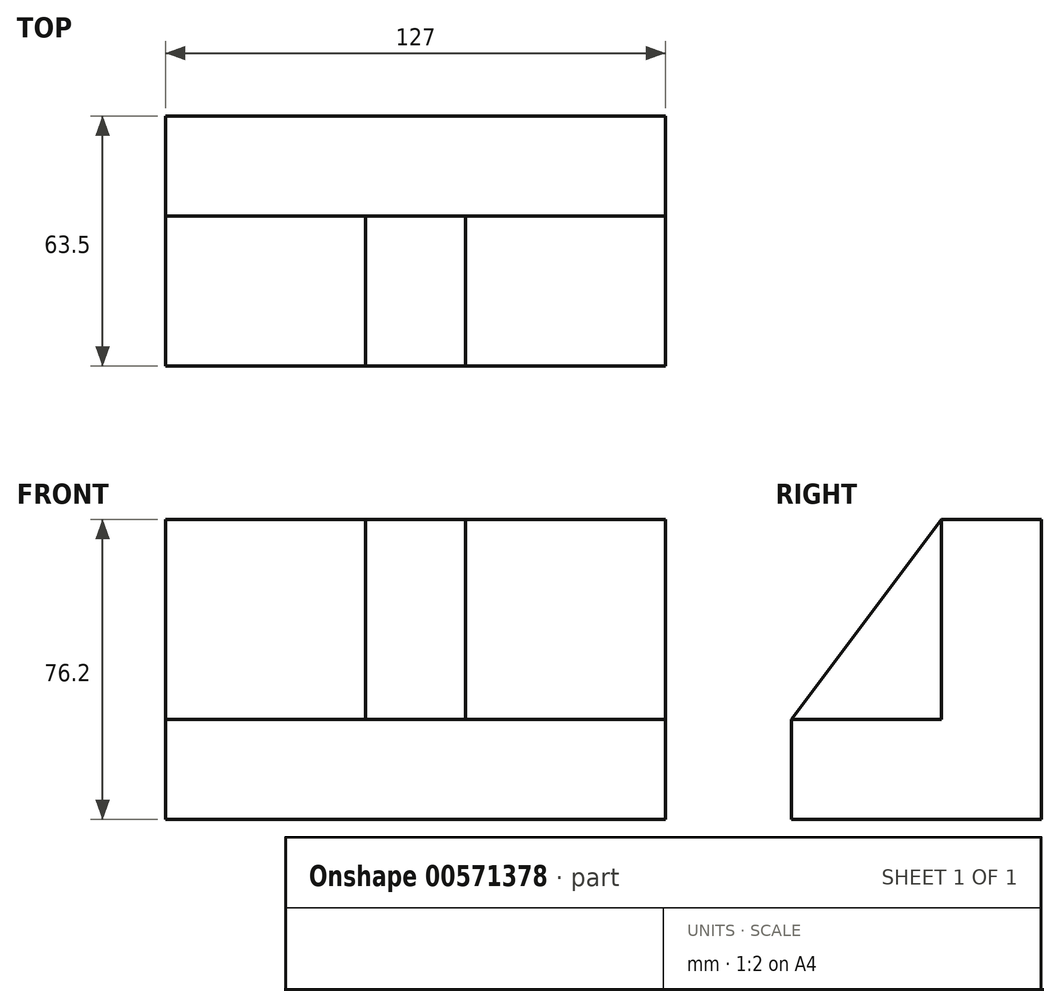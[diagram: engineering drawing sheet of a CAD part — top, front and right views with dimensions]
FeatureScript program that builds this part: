
annotation { "Feature Type Name" : "Feature", "Feature Type Description" : "" }
export const myFeature = defineFeature(function(context is Context, id is Id, definition is map)
    precondition{}
    {
        {
            var Q0;
            Q0=qCreatedBy(makeId("Front.planeOp"),FACE);
            var sketch = newSketch(context, id + "F0", { "sketchPlane" : qUnion([Q0])});
            skLineSegment(sketch, "E0.bottom", {"start": v(-94.95, 20.05) * mm, "end": v(32.05, 20.05) * mm});
            skLineSegment(sketch, "E0.top", {"start": v(-94.95, -56.15) * mm, "end": v(32.05, -56.15) * mm});
            skLineSegment(sketch, "E0.left", {"start": v(-94.95, 20.05) * mm, "end": v(-94.95, -56.15) * mm});
            skLineSegment(sketch, "E0.right", {"start": v(32.05, 20.05) * mm, "end": v(32.05, -56.15) * mm});
            skSolve(sketch);
        }
        {
            var Q0;
            Q0=makeQuery(id+"F0.imprint","IMPRINT",FACE,{"disambiguationData":[TD([[makeQuery(id+"F0.imprint","IMPRINT",EDGE,{"derivedFrom":sQuery(id+"F0.wireOp",EDGE,"E0.bottom")}),-1.0]])]});
            extrude(context, id + "F1", {"entities" : qUnion([Q0]), "depth" : 63.5 * mm, "offsetDistance" : 25.4 * mm});
        }
        {
            var Q0;
            Q0=makeQuery(id+"F1.opExtrude","SWEPT_FACE",FACE,{"disambiguationData":[OSD([sQuery(id+"F0.wireOp",EDGE,"E0.right")])]});
            var sketch = newSketch(context, id + "F2", { "sketchPlane" : qUnion([Q0])});
            skLineSegment(sketch, "E1", {"start": v(0, 20.05) * mm, "end": v(-25.4, 20.05) * mm});
            skLineSegment(sketch, "E2", {"start": v(-25.4, 20.05) * mm, "end": v(-25.4, -30.75) * mm});
            skLineSegment(sketch, "E3", {"start": v(-25.4, -30.75) * mm, "end": v(-63.5, -30.75) * mm});
            skPoint(sketch, "E3.endSnap0", {"position": v(-63.5, -18.05) * mm});
            skLineSegment(sketch, "E4", {"start": v(-63.5, -30.75) * mm, "end": v(-63.5, 20.05) * mm});
            skLineSegment(sketch, "E5", {"start": v(-63.5, 20.05) * mm, "end": v(-25.4, 20.05) * mm});
            skSolve(sketch);
        }
        {
            var Q0;
            Q0=makeQuery(id+"F2.imprint","IMPRINT",FACE,{"disambiguationData":[TD([[makeQuery(id+"F2.imprint","IMPRINT",EDGE,{"derivedFrom":sQuery(id+"F2.wireOp",EDGE,"E2")}),-1.0]])]});
            extrude(context, id + "F3", {"entities" : qUnion([Q0]), "operationType" : NewBodyOperationType.REMOVE, "oppositeDirection" : true, "depth" : 50.8 * mm, "offsetDistance" : 25.4 * mm});
        }
        {
            var Q0;
            Q0=makeQuery(id+"F1.opExtrude","SWEPT_FACE",FACE,{"disambiguationData":[OSD([sQuery(id+"F0.wireOp",EDGE,"E0.left")])]});
            var sketch = newSketch(context, id + "F4", { "sketchPlane" : qUnion([Q0])});
            skLineSegment(sketch, "E6", {"start": v(0, 20.05) * mm, "end": v(25.4, 20.05) * mm});
            skLineSegment(sketch, "E7", {"start": v(25.4, 20.05) * mm, "end": v(25.4, -30.75) * mm});
            skLineSegment(sketch, "E8", {"start": v(25.4, -30.75) * mm, "end": v(63.5, -30.75) * mm});
            skLineSegment(sketch, "E9", {"start": v(63.5, -30.75) * mm, "end": v(63.5, 20.05) * mm});
            skLineSegment(sketch, "E10", {"start": v(63.5, 20.05) * mm, "end": v(25.4, 20.05) * mm});
            skSolve(sketch);
        }
        {
            var Q0;
            Q0=makeQuery(id+"F4.imprint","IMPRINT",FACE,{"disambiguationData":[TD([[makeQuery(id+"F4.imprint","IMPRINT",EDGE,{"derivedFrom":sQuery(id+"F4.wireOp",EDGE,"E7")}),1.0]])]});
            extrude(context, id + "F5", {"entities" : qUnion([Q0]), "operationType" : NewBodyOperationType.REMOVE, "oppositeDirection" : true, "depth" : 50.8 * mm, "offsetDistance" : 25.4 * mm});
        }
        {
            var Q0;
            Q0=makeQuery(id+"F5.boolean.opBoolean","COPY",FACE,{"derivedFrom":makeQuery(id+"F5.opExtrude","CAP_FACE",FACE,{"disambiguationData":[OSD([sQuery(id+"F4.wireOp",EDGE,"E7"),sQuery(id+"F4.wireOp",EDGE,"E8"),sQuery(id+"F4.wireOp",EDGE,"E9"),sQuery(id+"F4.wireOp",EDGE,"E10")])],"isStart":false})});
            var sketch = newSketch(context, id + "F6", { "sketchPlane" : qUnion([Q0])});
            skLineSegment(sketch, "E11", {"start": v(25.4, 20.05) * mm, "end": v(63.5, -30.75) * mm});
            skLineSegment(sketch, "E12", {"start": v(63.5, -30.75) * mm, "end": v(63.5, 20.05) * mm});
            skLineSegment(sketch, "E13", {"start": v(63.5, 20.05) * mm, "end": v(25.4, 20.05) * mm});
            skSolve(sketch);
        }
        {
            var Q0;
            Q0=makeQuery(id+"F6.imprint","IMPRINT",FACE,{"disambiguationData":[TD([[makeQuery(id+"F6.imprint","IMPRINT",EDGE,{"derivedFrom":sQuery(id+"F6.wireOp",EDGE,"E11")}),1.0]])]});
            extrude(context, id + "F7", {"entities" : qUnion([Q0]), "operationType" : NewBodyOperationType.REMOVE, "endBound" : BoundingType.THROUGH_ALL, "oppositeDirection" : true, "depth" : 25.4 * mm, "offsetDistance" : 25.4 * mm});
        }
    });
